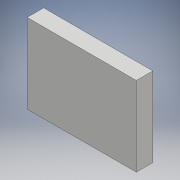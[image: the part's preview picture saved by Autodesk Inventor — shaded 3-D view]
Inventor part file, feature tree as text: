
AUTODESK INVENTOR PART (.ipt)
format: ipt  version: 2018 (Build 220112000, 112)  size: 88,064 bytes
history: native  units: mm
features: sketch x2, extrude x1
ambient origin geometry x8: Origin, YZ Plane, XZ Plane, XY Plane, X Axis, Y Axis, Z Axis, Center Point
bodies: 实体1 (feature_tree)
feature tree (3):
  extrude  "拉伸1"  Depth=33.0mm
  sketch  "草图2"  dims[d2=5.0mm d3=0.0mm]
  sketch  "草图1"  dims[d0=24.0mm d1=33.0mm]
